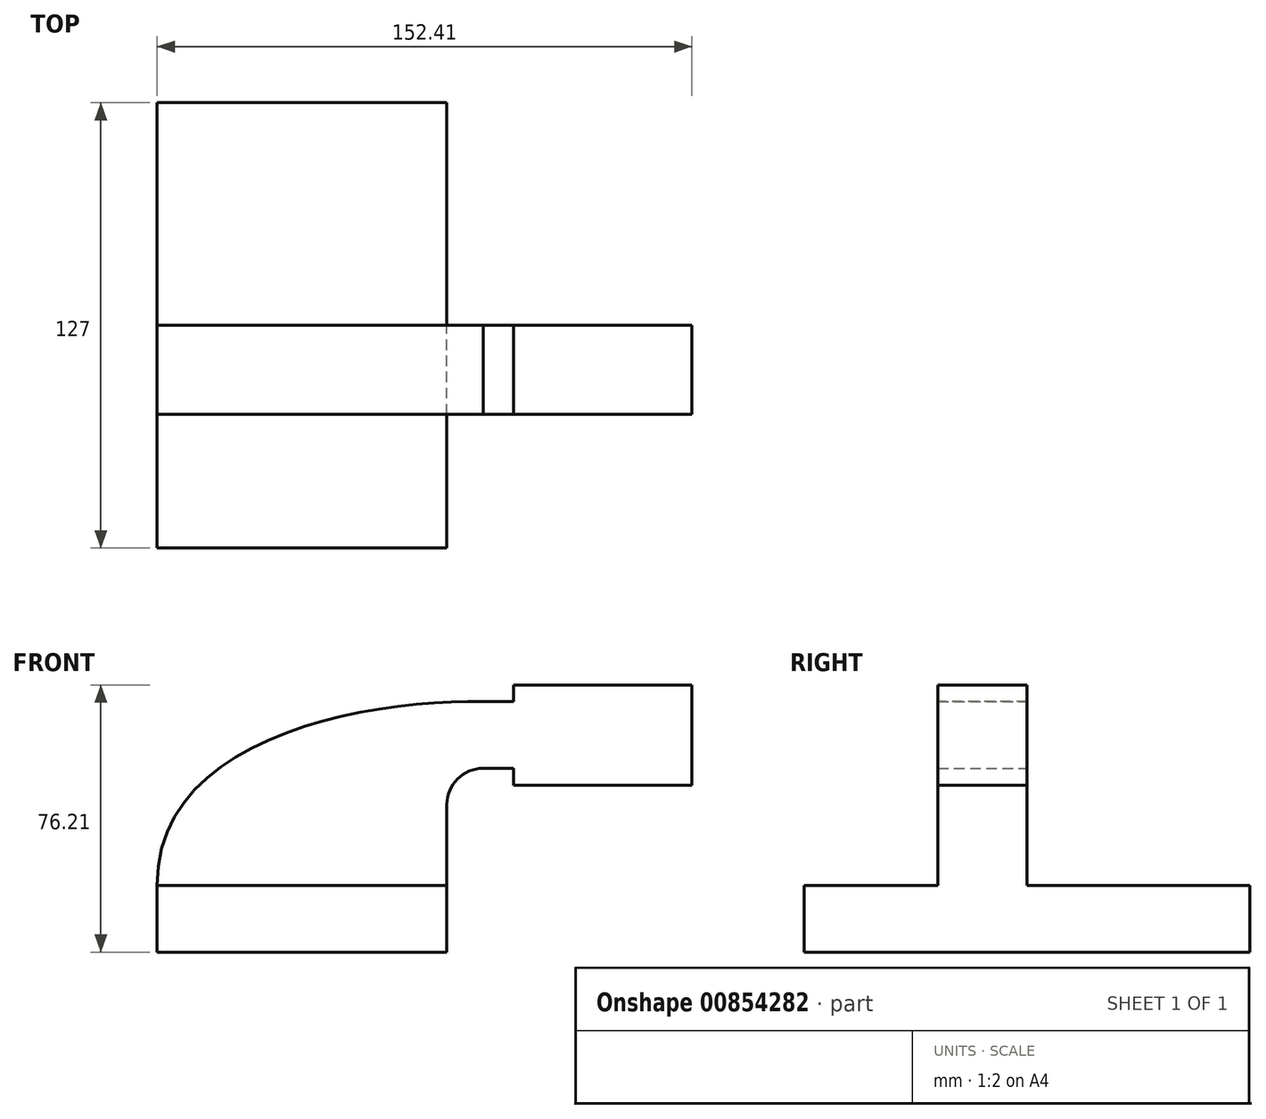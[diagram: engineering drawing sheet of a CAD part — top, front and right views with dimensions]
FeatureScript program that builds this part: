
annotation { "Feature Type Name" : "Feature", "Feature Type Description" : "" }
export const myFeature = defineFeature(function(context is Context, id is Id, definition is map)
    precondition{}
    {
        {
            var Q0;
            Q0=qCreatedBy(makeId("Front.planeOp"),FACE);
            var sketch = newSketch(context, id + "F0", { "sketchPlane" : qUnion([Q0])});
            skLineSegment(sketch, "E0.bottom", {"start": v(41.28, -9.52) * mm, "end": v(-41.28, -9.53) * mm});
            skLineSegment(sketch, "E0.top", {"start": v(41.28, 9.53) * mm, "end": v(-41.28, 9.53) * mm});
            skLineSegment(sketch, "E0.left", {"start": v(41.28, -9.52) * mm, "end": v(41.28, 9.53) * mm});
            skLineSegment(sketch, "E0.right", {"start": v(-41.28, -9.53) * mm, "end": v(-41.28, 9.53) * mm});
            skPoint(sketch, "E0.middle", {"position": v(0, 0) * mm});
            skLineSegment(sketch, "E1.bottom", {"start": v(60.32, 38.1) * mm, "end": v(111.12, 38.1) * mm});
            skLineSegment(sketch, "E1.top", {"start": v(60.32, 66.68) * mm, "end": v(111.12, 66.68) * mm});
            skLineSegment(sketch, "E1.left", {"start": v(60.32, 38.1) * mm, "end": v(60.32, 66.68) * mm});
            skLineSegment(sketch, "E1.right", {"start": v(111.12, 38.1) * mm, "end": v(111.12, 66.68) * mm});
            skPoint(sketch, "E1.middle", {"position": v(85.72, 52.39) * mm});
            skLineSegment(sketch, "E2", {"start": v(41.28, -7.8) * mm, "end": v(41.28, 9.53) * mm});
            skPoint(sketch, "E3.endSnap0", {"position": v(85.72, 38.1) * mm});
            skLineSegment(sketch, "E4", {"start": v(41.28, 9.53) * mm, "end": v(41.28, 32.53) * mm});
            skArc(sketch, "E5", {"start": v(41.27, 32.53) * mm, "mid": v(44.3, 39.84) * mm, "end": v(51.62, 42.88) * mm});
            skLineSegment(sketch, "E6", {"start": v(51.62, 42.88) * mm, "end": v(82.31, 42.88) * mm});
            skLineSegment(sketch, "E7.0", {"start": v(51.62, 61.93) * mm, "end": v(82.31, 61.93) * mm});
            skArc(sketch, "E7.1", {"start": v(22.22, 32.53) * mm, "mid": v(30.84, 53.32) * mm, "end": v(51.62, 61.93) * mm});
            skLineSegment(sketch, "E7.2", {"start": v(22.22, 9.53) * mm, "end": v(22.22, 32.53) * mm});
            skLineSegment(sketch, "E8", {"start": v(82.33, 38.1) * mm, "end": v(82.31, 66.68) * mm});
            skPoint(sketch, "E9.2.internal.snap0", {"position": v(66.97, 42.88) * mm});
            skFitSpline(sketch, "E10", {"points": [v(-41.28, 9.53) * mm, v(51.62, 61.93) * mm], "startDerivative": vector(-0.62, 128.35) * mm, "endDerivative": vector(97.67, -1.62) * mm});
            skSolve(sketch);
        }
        {
            var Q0;
            Q0=makeQuery(id+"F0.imprint","IMPRINT",FACE,{"disambiguationData":[TD([[makeQuery(id+"F0.imprint","IMPRINT",EDGE,{"derivedFrom":sQuery(id+"F0.wireOp",EDGE,"E0.bottom")}),-1.0]])]});
            extrude(context, id + "F1", {"entities" : qUnion([Q0]), "endBound" : BoundingType.SYMMETRIC, "depth" : 127 * mm, "offsetDistance" : 25.4 * mm});
        }
        {
            var Q0;
            Q0 = qSketchRegion(id + "F0", true);
            extrude(context, id + "F2", {"entities" : qUnion([Q0]), "operationType" : NewBodyOperationType.ADD, "depth" : 25.4 * mm, "offsetDistance" : 25.4 * mm});
        }
    });
